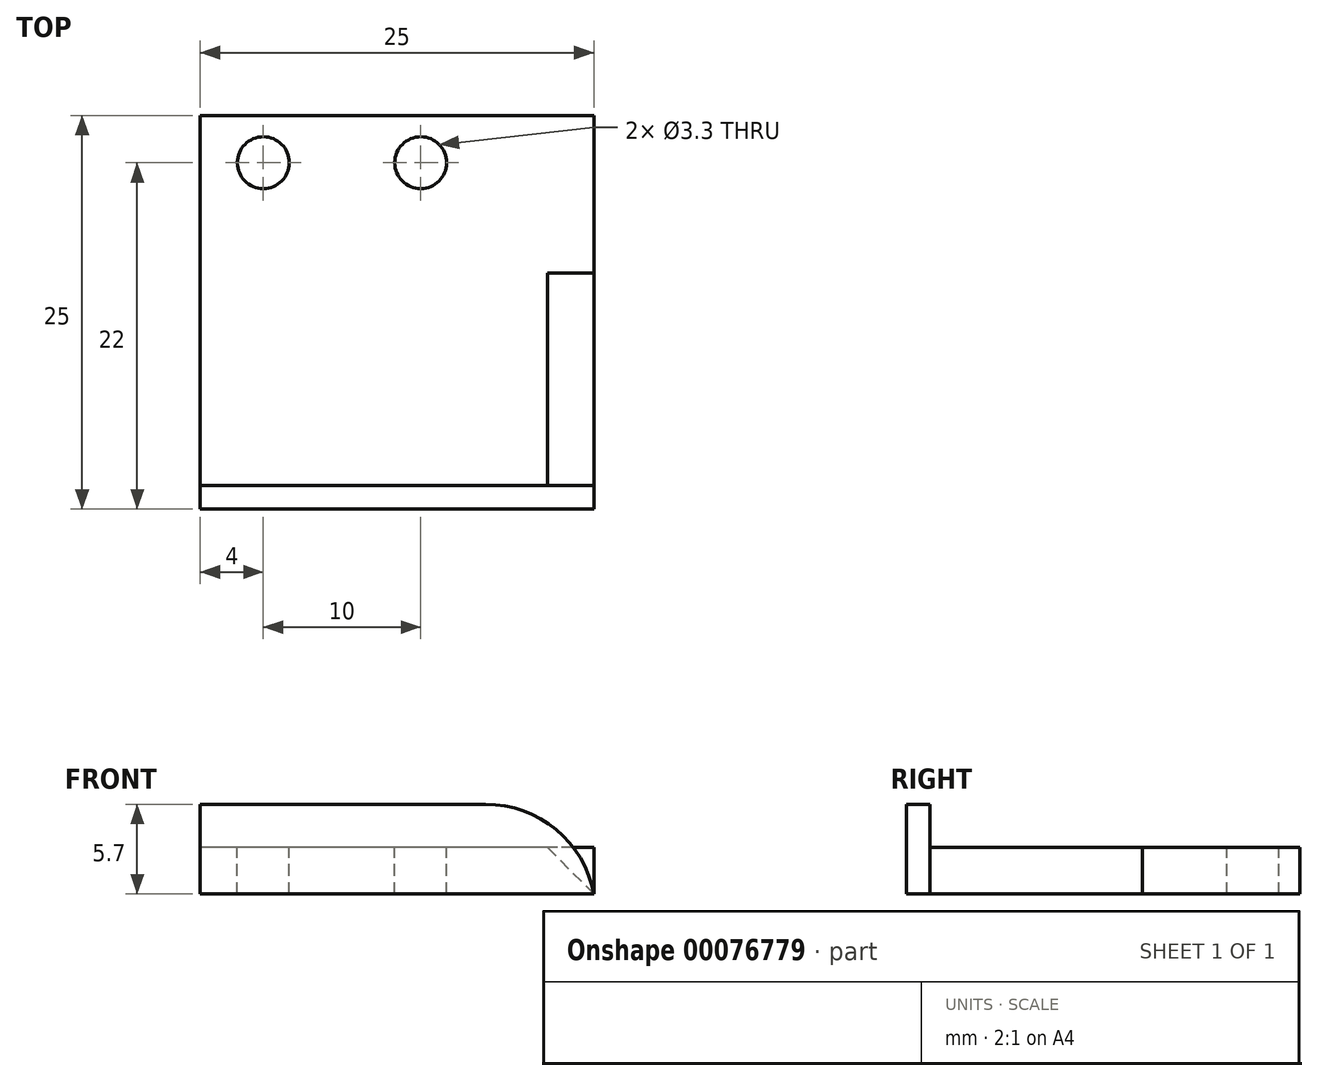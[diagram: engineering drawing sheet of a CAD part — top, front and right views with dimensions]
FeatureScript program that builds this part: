
annotation { "Feature Type Name" : "Feature", "Feature Type Description" : "" }
export const myFeature = defineFeature(function(context is Context, id is Id, definition is map)
    precondition{}
    {
        {
            var Q0;
            Q0=qCreatedBy(makeId("Top.planeOp"),FACE);
            var sketch = newSketch(context, id + "F0", { "sketchPlane" : qUnion([Q0])});
            skLineSegment(sketch, "E0.bottom", {"start": v(-12.5, 25) * mm, "end": v(12.5, 25) * mm});
            skLineSegment(sketch, "E0.top", {"start": v(-12.5, 0) * mm, "end": v(12.5, 0) * mm});
            skLineSegment(sketch, "E0.left", {"start": v(-12.5, 25) * mm, "end": v(-12.5, 0) * mm});
            skLineSegment(sketch, "E0.right", {"start": v(12.5, 25) * mm, "end": v(12.5, 0) * mm});
            skLineSegment(sketch, "E1", {"start": v(0, 0) * mm, "end": v(0, 25) * mm});
            skSolve(sketch);
        }
        {
            var Q0;
            {var subQ0=sQuery(id+"F0.wireOp",EDGE,"E0.left");Q0=makeQuery(id+"F0.imprint","IMPRINT",FACE,{"disambiguationData":[TD([[makeQuery(id+"F0.imprint","IMPRINT",EDGE,{"derivedFrom":subQ0}),1.0]])]});}
            var Q1;
            {var subQ0=sQuery(id+"F0.wireOp",EDGE,"E0.right");Q1=makeQuery(id+"F0.imprint","IMPRINT",FACE,{"disambiguationData":[TD([[makeQuery(id+"F0.imprint","IMPRINT",EDGE,{"derivedFrom":subQ0}),-1.0]])]});}
            extrude(context, id + "F1", {"entities" : qUnion([Q0, Q1]), "depth" : (7.5 - 1.8) * mm});
        }
        {
            var Q0;
            Q0=makeQuery(id+"F1.opExtrude","SWEPT_FACE",FACE,{"disambiguationData":[OSD([sQuery(id+"F0.wireOp",EDGE,"E0.left")])]});
            var sketch = newSketch(context, id + "F2", { "sketchPlane" : qUnion([Q0])});
            skLineSegment(sketch, "E2.bottom", {"start": v(-25, 5.7) * mm, "end": v(-1.5, 5.7) * mm});
            skLineSegment(sketch, "E2.top", {"start": v(-25, 2.95) * mm, "end": v(-1.5, 2.95) * mm});
            skLineSegment(sketch, "E2.left", {"start": v(-25, 5.7) * mm, "end": v(-25, 2.95) * mm});
            skLineSegment(sketch, "E2.right", {"start": v(-1.5, 5.7) * mm, "end": v(-1.5, 2.95) * mm});
            skSolve(sketch);
        }
        {
            var Q0;
            Q0=makeQuery(id+"F2.imprint","IMPRINT",FACE,{"disambiguationData":[TD([[makeQuery(id+"F2.imprint","IMPRINT",EDGE,{"derivedFrom":sQuery(id+"F2.wireOp",EDGE,"E2.bottom")}),-1.0]])]});
            extrude(context, id + "F3", {"entities" : qUnion([Q0]), "operationType" : NewBodyOperationType.REMOVE, "endBound" : BoundingType.THROUGH_ALL, "oppositeDirection" : true, "depth" : 25 * mm});
        }
        {
            var Q0;
            Q0=makeQuery(id+"F3.boolean.opBoolean","COPY",FACE,{"derivedFrom":makeQuery(id+"F3.opExtrude","SWEPT_FACE",FACE,{"disambiguationData":[OSD([sQuery(id+"F2.wireOp",EDGE,"E2.right")])]})});
            var sketch = newSketch(context, id + "F4", { "sketchPlane" : qUnion([Q0])});
            skLineSegment(sketch, "E3", {"start": v(-12.5, 2.95) * mm, "end": v(-9.55, 2.95) * mm});
            skLineSegment(sketch, "E4", {"start": v(-9.55, 2.95) * mm, "end": v(-12.5, 0) * mm});
            skLineSegment(sketch, "E5", {"start": v(-12.5, 0) * mm, "end": v(-12.5, 2.95) * mm});
            skSolve(sketch);
        }
        {
            var Q0;
            Q0=makeQuery(id+"F4.imprint","IMPRINT",FACE,{"disambiguationData":[TD([[makeQuery(id+"F4.imprint","IMPRINT",EDGE,{"derivedFrom":sQuery(id+"F4.wireOp",EDGE,"E3")}),-1.0]])]});
            extrude(context, id + "F5", {"entities" : qUnion([Q0]), "operationType" : NewBodyOperationType.REMOVE, "depth" : 13.5 * mm});
        }
        {
            var Q0;
            Q0=makeQuery(id+"F1.opExtrude","CAP_EDGE",EDGE,{"disambiguationData":[OSD([sQuery(id+"F0.wireOp",EDGE,"E0.right")])],"isStart":false});
            fillet(context, id + "F6", {"entities" : qUnion([Q0]), "radius" : 7 * mm, "tangentPropagation" : true, "allowEdgeOverflow" : false});
        }
        {
            var Q0;
            Q0=makeQuery(id+"F3.boolean.opBoolean","COPY",FACE,{"derivedFrom":makeQuery(id+"F3.opExtrude","SWEPT_FACE",FACE,{"disambiguationData":[OSD([sQuery(id+"F2.wireOp",EDGE,"E2.top")])]})});
            var sketch = newSketch(context, id + "F7", { "sketchPlane" : qUnion([Q0])});
            skCircle(sketch, "E6", {"center": v(-8.5, 22) * mm, "radius": 1.65 * mm});
            skCircle(sketch, "E7", {"center": v(1.5, 22) * mm, "radius": 1.65 * mm});
            skSolve(sketch);
        }
        {
            var Q0;
            Q0=makeQuery(id+"F7.imprint","IMPRINT",FACE,{"disambiguationData":[TD([[makeQuery(id+"F7.imprint","IMPRINT",EDGE,{"derivedFrom":sQuery(id+"F7.wireOp",EDGE,"E6")}),1.0]])]});
            var Q1;
            Q1=makeQuery(id+"F7.imprint","IMPRINT",FACE,{"disambiguationData":[TD([[makeQuery(id+"F7.imprint","IMPRINT",EDGE,{"derivedFrom":sQuery(id+"F7.wireOp",EDGE,"E7")}),1.0]])]});
            extrude(context, id + "F8", {"entities" : qUnion([Q0, Q1]), "operationType" : NewBodyOperationType.REMOVE, "oppositeDirection" : true, "depth" : 25 * mm});
        }
    });
